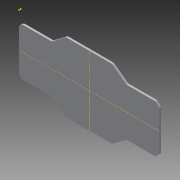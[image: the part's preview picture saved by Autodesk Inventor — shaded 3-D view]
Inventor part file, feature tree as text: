
AUTODESK INVENTOR PART (.ipt)
format: ipt  version: 2015 (Build 190159000, 159)  size: 132,608 bytes
history: native  units: mm
features: sketch x6, extrude x3, fillet x3, plane x3, mirror x2, chamfer x1
ambient origin geometry x8: Origin, YZ Plane, XZ Plane, XY Plane, X Axis, Y Axis, Z Axis, Center Point
bodies: Solid1 (feature_tree)
feature tree (18):
  extrude  "Extrusion1"  Depth=148.0mm
  sketch  "Sketch2"  dims[d2=4.0mm d3=0.0mm d4=70.0mm d5=23.0mm]
  extrude  "Extrusion2"  Depth=23.0mm
  fillet  "Fillet1"  Radius=23.0mm
  extrude  "Extrusion3"  Depth=10.0mm
  plane  "Work Plane1"
  plane  "Work Plane2"
  mirror  "Mirror2"
  fillet  "Fillet2"  Radius=10.0mm
  sketch  "Sketch6"
  plane  "Work Plane3"
  mirror  "Mirror3"
  chamfer  "Chamfer1"  Distance=8.0mm Angle=45.0deg
  fillet  "Fillet3"  Radius=8.0mm
  sketch  "Sketch7"
  sketch  "Sketch1"  dims[d0=300.0mm d1=148.0mm]
  sketch  "Sketch3"  dims[d6=10.0mm d7=0.0mm d8=10.0mm d9=10.0mm d10=0.0mm]
  sketch  "Sketch4"  dims[d11=10.0mm d14=8.0mm d15=2.0mm d16=45.0deg d17=8.0mm]
